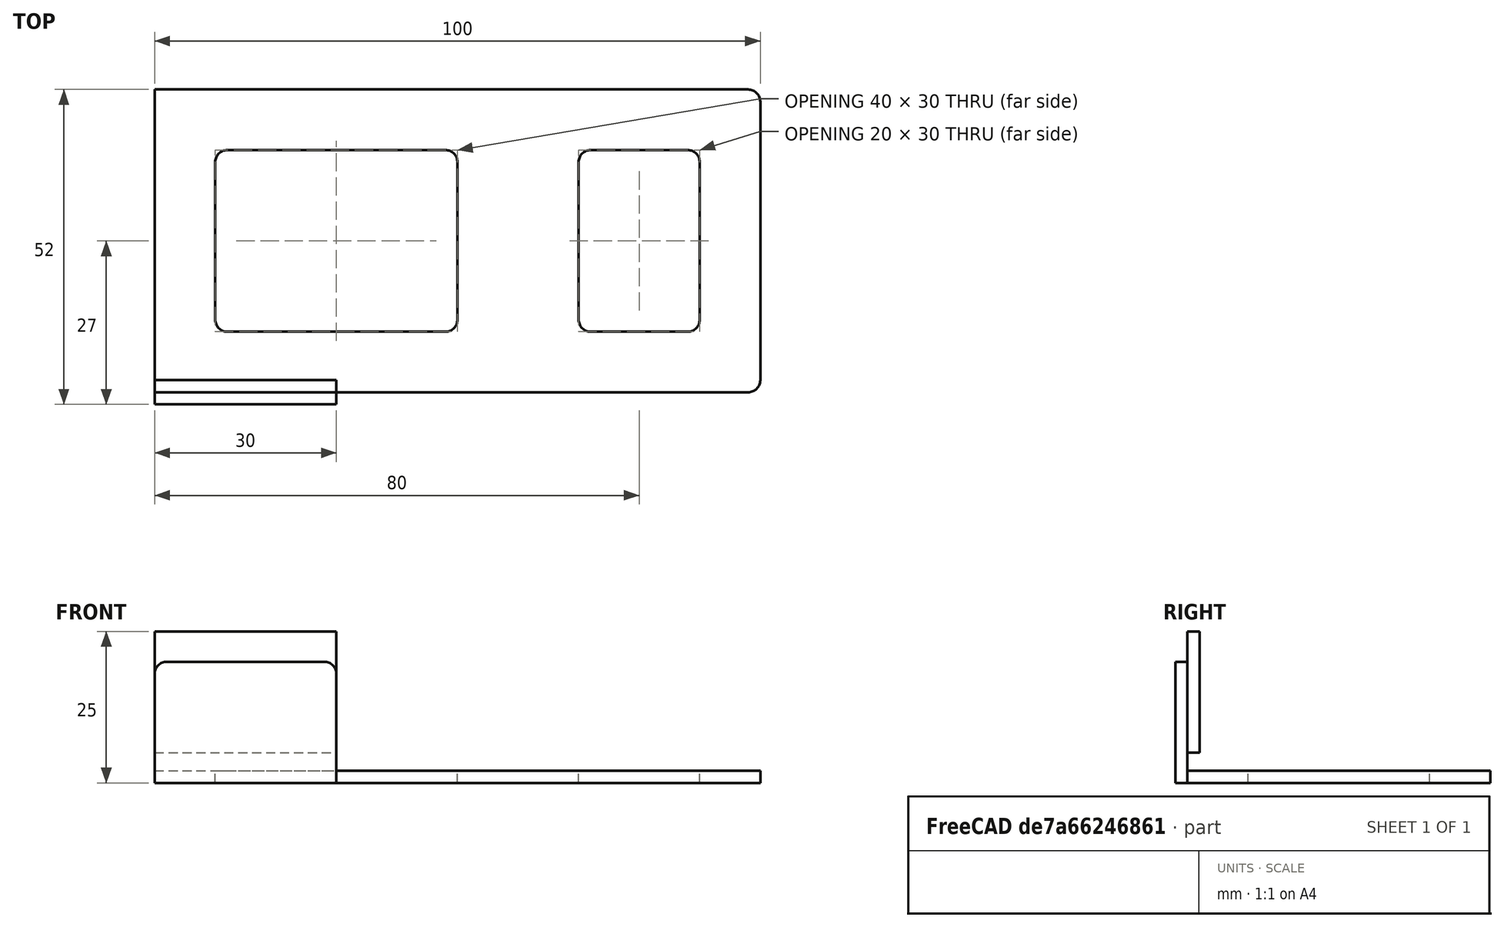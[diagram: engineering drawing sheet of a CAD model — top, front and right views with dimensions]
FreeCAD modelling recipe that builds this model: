
FCSTD DOCUMENT  (FreeCAD 0.21R33694 (Git))
Label: OJT1_T12R03_hola
License: All rights reserved
LicenseURL: https://en.wikipedia.org/wiki/All_rights_reserved
objects: Part::Fillet×12, Part::Box×5, Part::Cut×2
note: 19 computed .brp shape members not serialized (recipe doc carries the construction recipe); baked Part::Feature solids carry a one-line shape summary decoded from their .brp

FEATURE [Part::Box] Box  label="Cub"
  AttacherType = Attacher::AttachEngine3D
  Height = 2
  Length = 100
  Width = 50
FEATURE [Part::Fillet] Fillet
  Base = -> Box
  Edges = 1 edges r=2: [Edge5]
FEATURE [Part::Fillet] Fillet001  label="Base_1"
  Base = -> Fillet
  Edges = 1 edges r=2: [Edge4]
FEATURE [Part::Box] Box001  label="Cub001"
  AttacherType = Attacher::AttachEngine3D
  Height = 2
  Length = 20
  Placement = pos=(70,10,6) rot=(0,0,1;0rad)
  Width = 30
FEATURE [Part::Fillet] Fillet002
  Base = -> Box001
  Edges = 1 edges r=2: [Edge5]
FEATURE [Part::Fillet] Fillet003
  Base = -> Fillet002
  Edges = 1 edges r=2: [Edge4]
FEATURE [Part::Fillet] Fillet004
  Base = -> Fillet003
  Edges = 1 edges r=2: [Edge18]
FEATURE [Part::Fillet] Fillet005  label="Forat_1"
  Base = -> Fillet004
  Edges = 1 edges r=2: [Edge10]
  Placement = pos=(0,0,-6) rot=(0,0,1;0rad)
FEATURE [Part::Cut] Cut
  Base = -> Fillet001
  Tool = -> Fillet005
FEATURE [Part::Box] Box002  label="Cub002"
  AttacherType = Attacher::AttachEngine3D
  Height = 2
  Length = 40
  Placement = pos=(10,10,4) rot=(0,0,1;0rad)
  Width = 30
FEATURE [Part::Fillet] Fillet006
  Base = -> Box002
  Edges = 1 edges r=2: [Edge7]
FEATURE [Part::Fillet] Fillet007
  Base = -> Fillet006
  Edges = 1 edges r=2: [Edge2]
FEATURE [Part::Fillet] Fillet008
  Base = -> Fillet007
  Edges = 1 edges r=2: [Edge17]
FEATURE [Part::Fillet] Fillet009
  Base = -> Fillet008
  Edges = 1 edges r=2: [Edge16]
  Placement = pos=(0,0,-4) rot=(0,0,1;0rad)
FEATURE [Part::Cut] Cut001  label="BASE"
  Base = -> Cut
  Tool = -> Fillet009
FEATURE [Part::Box] Box003  label="Cub003"
  AttacherType = Attacher::AttachEngine3D
  Height = 20
  Length = 30
  Width = 2
FEATURE [Part::Fillet] Fillet010
  Base = -> Box003
  Edges = 1 edges r=2: [Edge6]
FEATURE [Part::Fillet] Fillet011  label="Orella 1"
  Base = -> Fillet010
  Edges = 1 edges r=2: [Edge15]
  Placement = pos=(0,-2,0) rot=(0,0,1;0rad)
FEATURE [Part::Box] Box004  label="Cub004"
  AttacherType = Attacher::AttachEngine3D
  Height = 20
  Length = 30
  Placement = pos=(0,0,5) rot=(0,0,1;0rad)
  Width = 2
